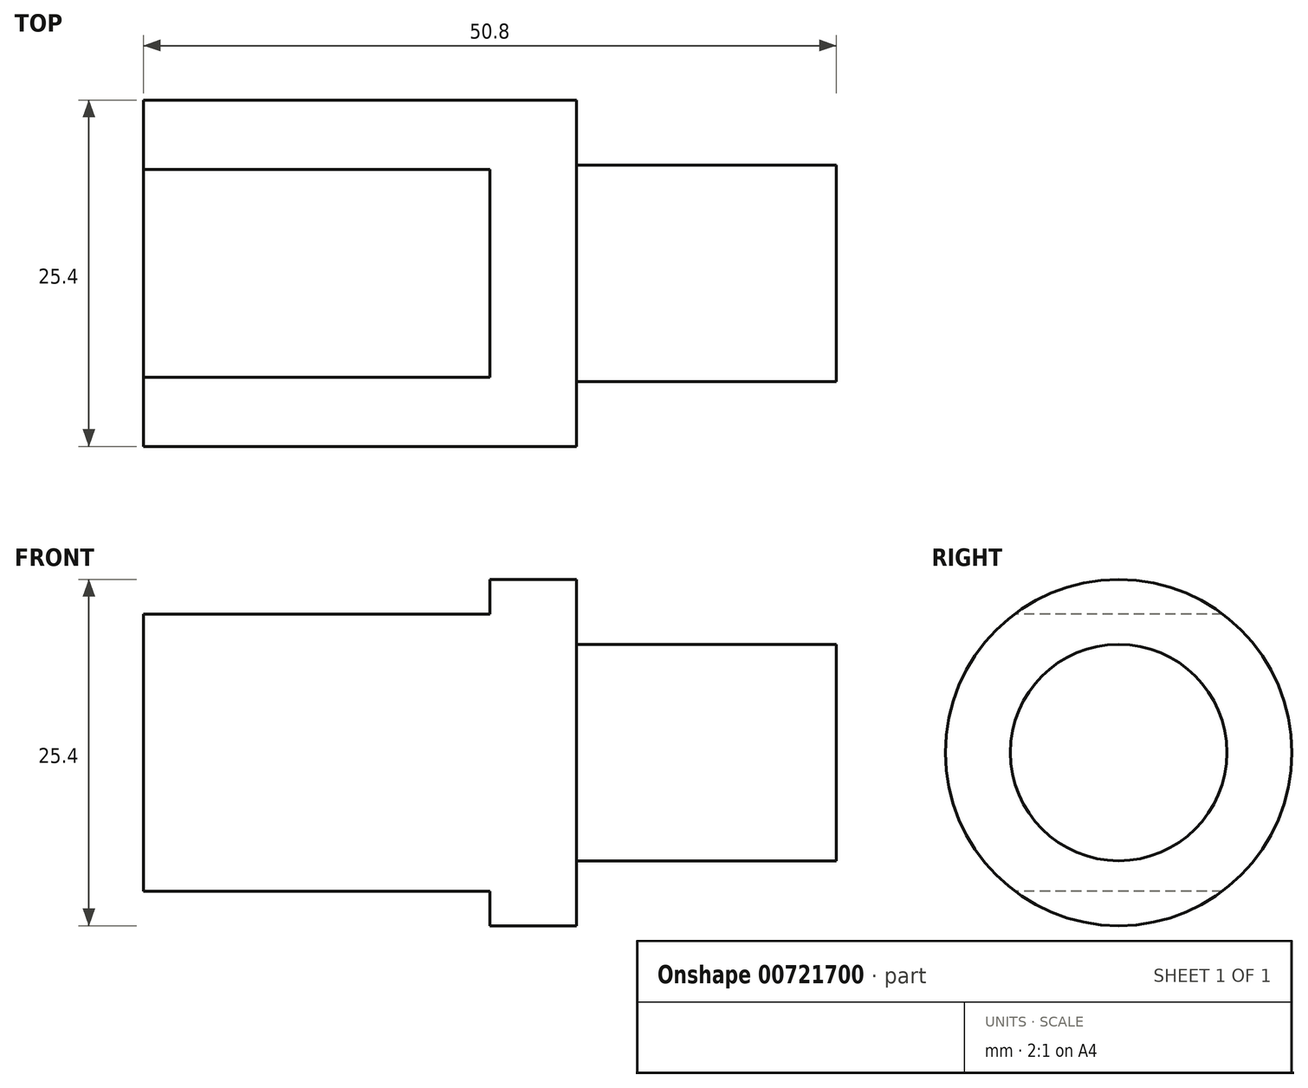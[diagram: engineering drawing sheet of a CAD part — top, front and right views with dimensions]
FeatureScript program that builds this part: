
annotation { "Feature Type Name" : "Feature", "Feature Type Description" : "" }
export const myFeature = defineFeature(function(context is Context, id is Id, definition is map)
    precondition{}
    {
        {
            var Q0;
            Q0=qCreatedBy(makeId("Front.planeOp"),FACE);
            var sketch = newSketch(context, id + "F0", { "sketchPlane" : qUnion([Q0])});
            skLineSegment(sketch, "E0", {"start": v(0, 12.7) * mm, "end": v(31.75, 12.7) * mm});
            skLineSegment(sketch, "E1", {"start": v(31.75, 12.7) * mm, "end": v(31.75, 7.94) * mm});
            skLineSegment(sketch, "E2", {"start": v(31.75, 7.94) * mm, "end": v(50.8, 7.94) * mm});
            skLineSegment(sketch, "E3", {"start": v(50.8, 7.94) * mm, "end": v(50.8, 0) * mm});
            skLineSegment(sketch, "E4", {"start": v(50.8, 0) * mm, "end": v(0, 0) * mm});
            skLineSegment(sketch, "E5", {"start": v(0, 0) * mm, "end": v(0, 12.7) * mm});
            skLineSegment(sketch, "E6", {"start": v(-24.53, 0) * mm, "end": v(74.02, 0) * mm, "construction": true});
            skSolve(sketch);
        }
        {
            var Q0;
            Q0=qSketchRegion(id+"F0",true);
            var Q1;
            Q1=sQuery(id+"F0.wireOp",EDGE,"E6");
            revolve(context, id + "F1", {"surfaceOperationType" : NewSurfaceOperationType.NEW, "entities" : qUnion([Q0]), "axis" : qUnion([Q1]), "revolveType" : RevolveType.FULL});
        }
        {
            var Q0;
            Q0=makeQuery(id+"F1.opRevolve","SWEPT_FACE",FACE,{"disambiguationData":[OSD([sQuery(id+"F0.wireOp",EDGE,"E5")])]});
            var sketch = newSketch(context, id + "F2", { "sketchPlane" : qUnion([Q0])});
            skLineSegment(sketch, "E7", {"start": v(-7.62, 10.16) * mm, "end": v(7.62, 10.16) * mm});
            skLineSegment(sketch, "E8", {"start": v(-20.41, 0) * mm, "end": v(21.4, 0) * mm, "construction": true});
            skArc(sketch, "E9", {"start": v(7.62, 10.16) * mm, "mid": v(0, 12.7) * mm, "end": v(-7.62, 10.16) * mm});
            skLineSegment(sketch, "E10.MirrorCS", {"start": v(-7.62, -10.16) * mm, "end": v(7.62, -10.16) * mm});
            skArc(sketch, "E11.MirrorCS", {"start": v(7.62, -10.16) * mm, "mid": v(0, -12.7) * mm, "end": v(-7.62, -10.16) * mm});
            skSolve(sketch);
        }
        {
            var Q0;
            Q0=qSketchRegion(id+"F2",true);
            extrude(context, id + "F3", {"entities" : qUnion([Q0]), "operationType" : NewBodyOperationType.REMOVE, "oppositeDirection" : true, "depth" : 25.4 * mm, "offsetDistance" : 25.4 * mm});
        }
    });
